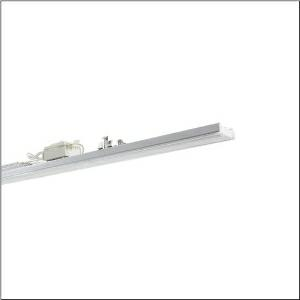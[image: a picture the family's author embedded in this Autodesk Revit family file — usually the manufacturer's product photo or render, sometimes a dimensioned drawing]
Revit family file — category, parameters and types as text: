
# Revit family: licross_r__21_recessed_mo_52tl11dn4axg3s4_e674
name_source: partatom
category: Lighting Fixtures
units: mm (PartAtom-declared; Revit-internal decimal feet)

## family parameters
Cut with Voids When Loaded = No
Host = Face
Light Source = No
Part Type = Normal
Room Calculation Point = No
Round Connector Dimension = Use Diameter
Shared = No

## types (1)
- --- (1 x LED, 930 lm, 6.7 W, 4000K)
    Apparent Load = 7 VA
    CIE Flux Codes = 89 96 99 100 100
    Color Rendering = 80
    Color Temperature = 4000K
    Default Elevation = 1800 mm
    Description = Licross® 21 Recessed MO, luminaire insert, of sheet steel, galvanised, coil coated, white, length: 1.500mm, width: 66mm, height: 67mm, LED rated luminous flux: 10.120lm, light colour: 840, control gear: DALI 2, with plug, 6-pole, with phase selection, for trunking rail, 9 or 11-core, mains connection: 220..240V, AC, 50/60Hz, rated input power: 62W, for emergency light function, internal wiring halogen-free, for trunking rail, 9-/11-core, converter,control gear: single battery element, battery: LiFePO4, 9Ah, primary optical cover: cover, of PMMA, light emission: direct distribution, primary light characteristic: symmetric, protection rating (complete): IP40, insulation class (complete): insulation class I (protective earthing), certification: CE, UKCA, protection symbol: D if used in an environment without relevant dust loads with corresponding accessories, impact resistance: IK06, permissible ambient temperature for indoor applications: +5..+35°C, standard: EN 60598-2-22, corresponds to IFS (International Featured Standards) requirements for safety and quality in the food industry, reducing of maximum allowable ambient temperature of 5°C with ceiling mounting, LABS conformity tested according to VDMA 24364:2018-05, packaging unit: 1 piece
    Height = 58 mm
    Lamp = 1 x LED
    Lamp Light Flux = 930 lm
    Lamp Power = 6.7 W
    Lamp count = 1
    Length = 1500 mm
    Luminous efficacy = 139 lm/W
    Manufacturer = Siteco
    ModVariant = No
    Model = 52TL11DN4AXG3S4
    Mounting Place = Ceiling
    Mounting Type = Pendant
    Number of Poles = 1
    OnlyDefault = Yes
    Power Factor = 1
    Product Name = Licross® 21 Recessed MO
    Product group = luminaire insert | ceiling pendant
    ProductGroupID = 902
    Protection Class = Protection class I
    Protection Degree = IP 40
    RLX_Detail_Level = 1
    RLX_Emergency_Light_Flux = 0 lm
    RLX_Emergency_Type = 0
    RLX_Emergency_Type_DB = No
    RlxData = <blob elided: 24909 chars, md5=c73a8c77>
    Socket = socket
    Standby Power = 0 W
    System Light Flux = 930 lm
    System Power = 7 W
    Type Comments = : emergency light operation: 3 h
    Type Image = l_1296930.jpg
    URL = http://relux.com
    VarID = @adj_132103
    Voltage = 0 V
    Weight = 0.00 kg
    Width = 66 mm

## geometry (parser evidence)
native form markers: Blend x4, Sweep x11
no freeform markers — native parametric forms only
